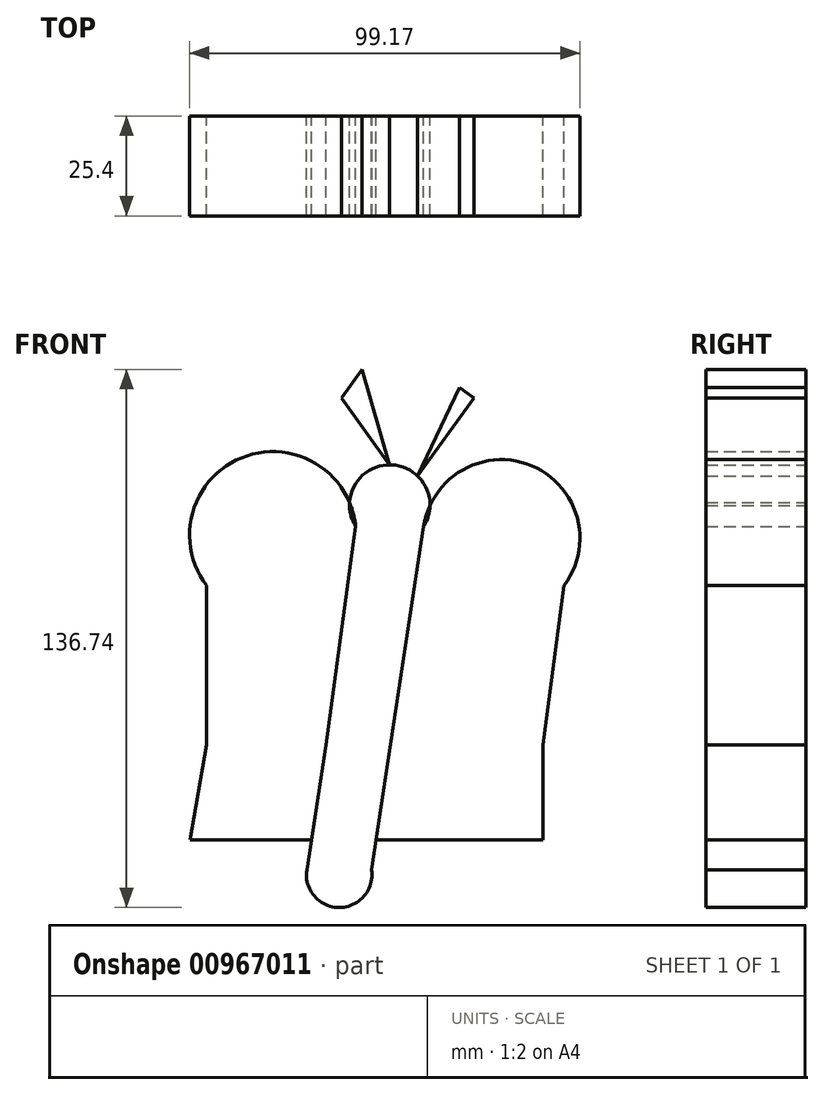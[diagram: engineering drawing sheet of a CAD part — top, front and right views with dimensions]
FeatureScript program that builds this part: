
annotation { "Feature Type Name" : "Feature", "Feature Type Description" : "" }
export const myFeature = defineFeature(function(context is Context, id is Id, definition is map)
    precondition{}
    {
        {
            var Q0;
            Q0=qCreatedBy(makeId("Front.planeOp"),FACE);
            var sketch = newSketch(context, id + "F0", { "sketchPlane" : qUnion([Q0])});
            skLineSegment(sketch, "E0", {"start": v(-50.6, 11.66) * mm, "end": v(-50.6, -28.86) * mm});
            skArc(sketch, "E1", {"start": v(-12.74, 26.7) * mm, "mid": v(-41.6, 44.2) * mm, "end": v(-50.6, 11.66) * mm});
            skArc(sketch, "E2", {"start": v(40.18, 11.66) * mm, "mid": v(32.03, 42.09) * mm, "end": v(4.54, 26.7) * mm});
            skLineSegment(sketch, "E3", {"start": v(40.18, 11.66) * mm, "end": v(34.78, -28.86) * mm});
            skLineSegment(sketch, "E4", {"start": v(-12.74, 26.7) * mm, "end": v(-20.3, -28.86) * mm});
            skLineSegment(sketch, "E5", {"start": v(4.54, 26.7) * mm, "end": v(-8.73, -60.57) * mm});
            skLineSegment(sketch, "E6", {"start": v(-20.3, -28.86) * mm, "end": v(-25.16, -60.57) * mm});
            skArc(sketch, "E7", {"start": v(4.54, 26.7) * mm, "mid": v(-4.1, 42.35) * mm, "end": v(-12.74, 26.7) * mm});
            skLineSegment(sketch, "E8", {"start": v(-4.1, 42.35) * mm, "end": v(-11.12, 66.6) * mm});
            skLineSegment(sketch, "E9", {"start": v(3.01, 39.47) * mm, "end": v(17.3, 59.35) * mm});
            skArc(sketch, "E10", {"start": v(-25.16, -60.57) * mm, "mid": v(-16.94, -70.15) * mm, "end": v(-8.73, -60.57) * mm});
            skLineSegment(sketch, "E11", {"start": v(-50.6, -28.86) * mm, "end": v(-54.86, -52.97) * mm});
            skLineSegment(sketch, "E12", {"start": v(-54.86, -52.97) * mm, "end": v(-24, -52.97) * mm});
            skLineSegment(sketch, "E13", {"start": v(-7.57, -52.97) * mm, "end": v(34.78, -52.97) * mm});
            skLineSegment(sketch, "E14", {"start": v(34.78, -52.97) * mm, "end": v(34.78, -28.86) * mm});
            skLineSegment(sketch, "E15", {"start": v(17.3, 59.35) * mm, "end": v(13.6, 62) * mm});
            skPoint(sketch, "E15.endSnap0", {"position": v(13.6, -52.97) * mm});
            skLineSegment(sketch, "E16", {"start": v(13.6, 62) * mm, "end": v(3.01, 39.47) * mm});
            skLineSegment(sketch, "E17", {"start": v(-11.12, 66.6) * mm, "end": v(-16.33, 59.35) * mm});
            skLineSegment(sketch, "E18", {"start": v(-16.33, 59.35) * mm, "end": v(-4.1, 42.35) * mm});
            skSolve(sketch);
        }
        {
            var Q0;
            {var subQ4=sQuery(id+"F0.wireOp",EDGE,"E0");Q0=makeQuery(id+"F0.imprint","IMPRINT",FACE,{"disambiguationData":[TD([[makeQuery(id+"F0.imprint","IMPRINT",EDGE,{"derivedFrom":subQ4}),1.0]])]});}
            var Q1;
            {var subQ6=sQuery(id+"F0.wireOp",EDGE,"E3");Q1=makeQuery(id+"F0.imprint","IMPRINT",FACE,{"disambiguationData":[TD([[makeQuery(id+"F0.imprint","IMPRINT",EDGE,{"derivedFrom":subQ6}),-1.0]])]});}
            var Q2;
            Q2=makeQuery(id+"F0.imprint","IMPRINT",FACE,{"disambiguationData":[TD([[makeQuery(id+"F0.imprint","IMPRINT",EDGE,{"derivedFrom":sQuery(id+"F0.wireOp",EDGE,"E8")}),1.0]])]});
            var Q3;
            Q3=makeQuery(id+"F0.imprint","IMPRINT",FACE,{"disambiguationData":[TD([[makeQuery(id+"F0.imprint","IMPRINT",EDGE,{"derivedFrom":sQuery(id+"F0.wireOp",EDGE,"E9")}),1.0]])]});
            extrude(context, id + "F1", {"entities" : qUnion([Q0, Q1, Q2, Q3]), "depth" : 25.4 * mm, "offsetDistance" : 25.4 * mm});
        }
        {
            var Q0;
            {var subQ8=sQuery(id+"F0.wireOp",EDGE,"E4");Q0=makeQuery(id+"F0.imprint","IMPRINT",FACE,{"disambiguationData":[TD([[makeQuery(id+"F0.imprint","IMPRINT",EDGE,{"derivedFrom":subQ8}),1.0]])]});}
            extrude(context, id + "F2", {"entities" : qUnion([Q0]), "depth" : 25.4 * mm, "offsetDistance" : 25.4 * mm});
        }
    });
